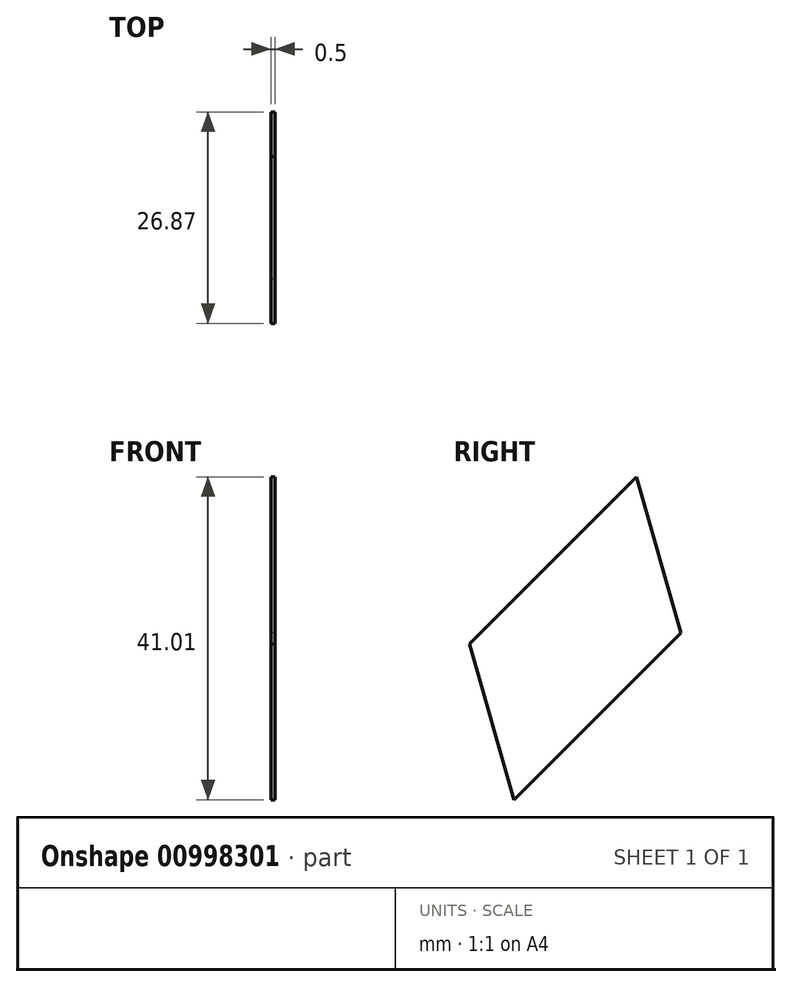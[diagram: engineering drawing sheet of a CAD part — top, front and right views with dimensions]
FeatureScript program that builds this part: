
annotation { "Feature Type Name" : "Feature", "Feature Type Description" : "" }
export const myFeature = defineFeature(function(context is Context, id is Id, definition is map)
    precondition{}
    {
        {
            var Q0;
            Q0=qCreatedBy(makeId("Right.planeOp"),FACE);
            var sketch = newSketch(context, id + "F0", { "sketchPlane" : qUnion([Q0])});
            skLineSegment(sketch, "E0", {"start": v(0, 0) * mm, "end": v(0, -28.99) * mm, "construction": true});
            skLineSegment(sketch, "E1", {"start": v(-30, -18) * mm, "end": v(0, -18) * mm});
            skLineSegment(sketch, "E2", {"start": v(-30, -18) * mm, "end": v(-20, 0) * mm});
            skLineSegment(sketch, "E3", {"start": v(-20, 0) * mm, "end": v(0, 0) * mm});
            skLineSegment(sketch, "E4", {"start": v(0, -18) * mm, "end": v(10, 0) * mm});
            skLineSegment(sketch, "E5", {"start": v(0, 0) * mm, "end": v(10, 0) * mm});
            skSolve(sketch);
        }
        {
            var Q0;
            Q0=makeQuery(id+"F0.imprint","IMPRINT",FACE,{"disambiguationData":[TD([[makeQuery(id+"F0.imprint","IMPRINT",EDGE,{"derivedFrom":sQuery(id+"F0.wireOp",EDGE,"E1")}),1.0]])]});
            extrude(context, id + "F1", {"entities" : qUnion([Q0]), "depth" : 0.5 * mm, "offsetDistance" : 25 * mm});
        }
        {
            var Q0;
            Q0=qCreatedBy(makeId("Right.planeOp"),FACE);
            var sketch = newSketch(context, id + "F2", { "sketchPlane" : qUnion([Q0])});
            skLineSegment(sketch, "E6", {"start": v(0, 0) * mm, "end": v(0, -95) * mm, "construction": true});
            skSolve(sketch);
        }
        {
            var Q0;
            Q0=makeQuery(id+"F1.opExtrude","SWEPT_BODY",BODY,{"disambiguationData":[OSD([sQuery(id+"F0.wireOp",EDGE,"E1"),sQuery(id+"F0.wireOp",EDGE,"E2"),sQuery(id+"F0.wireOp",EDGE,"E3"),sQuery(id+"F0.wireOp",EDGE,"E4"),sQuery(id+"F0.wireOp",EDGE,"E5")])]});
            var Q1;
            Q1=makeQuery(id+"F1.opExtrude","CAP_VERTEX",VERTEX,{"disambiguationData":[OSD([sQuery(id+"F0.wireOp",EDGE,"E1"),sQuery(id+"F0.wireOp",EDGE,"E2")])],"isStart":false});
            var Q2;
            Q2=sQuery(id+"F2.wireOp",VERTEX,"E6.end");
            transform(context, id + "F3", {"entities" : qUnion([Q0]), "transformType" : TransformType.TRANSLATION_ENTITY, "oppositeDirectionEntity" : false, "transformLine" : qUnion([Q1, Q2]), "makeCopy" : false});
        }
        {
            var Q0;
            Q0=makeQuery(id+"F1.opExtrude","SWEPT_BODY",BODY,{"disambiguationData":[OSD([sQuery(id+"F0.wireOp",EDGE,"E1"),sQuery(id+"F0.wireOp",EDGE,"E2"),sQuery(id+"F0.wireOp",EDGE,"E3"),sQuery(id+"F0.wireOp",EDGE,"E4"),sQuery(id+"F0.wireOp",EDGE,"E5")])]});
            var Q1;
            Q1=makeQuery(id+"F1.opExtrude","SWEPT_EDGE",EDGE,{"disambiguationData":[OSD([sQuery(id+"F0.wireOp",EDGE,"E1"),sQuery(id+"F0.wireOp",EDGE,"E2")])]});
            transform(context, id + "F4", {"entities" : qUnion([Q0]), "transformType" : TransformType.ROTATION, "transformAxis" : qUnion([Q1]), "angle" : 45 * degree, "oppositeDirection" : true, "makeCopy" : false});
        }
        {
            var Q0;
            Q0=makeQuery(id+"F1.opExtrude","SWEPT_BODY",BODY,{"disambiguationData":[OSD([sQuery(id+"F0.wireOp",EDGE,"E1"),sQuery(id+"F0.wireOp",EDGE,"E2"),sQuery(id+"F0.wireOp",EDGE,"E3"),sQuery(id+"F0.wireOp",EDGE,"E4"),sQuery(id+"F0.wireOp",EDGE,"E5")])]});
            transform(context, id + "F5", {"entities" : qUnion([Q0]), "transformType" : TransformType.TRANSLATION_3D, "dx" : 0 * mm, "dy" : -3 * mm, "dz" : 0 * mm, "makeCopy" : false});
        }
    });
